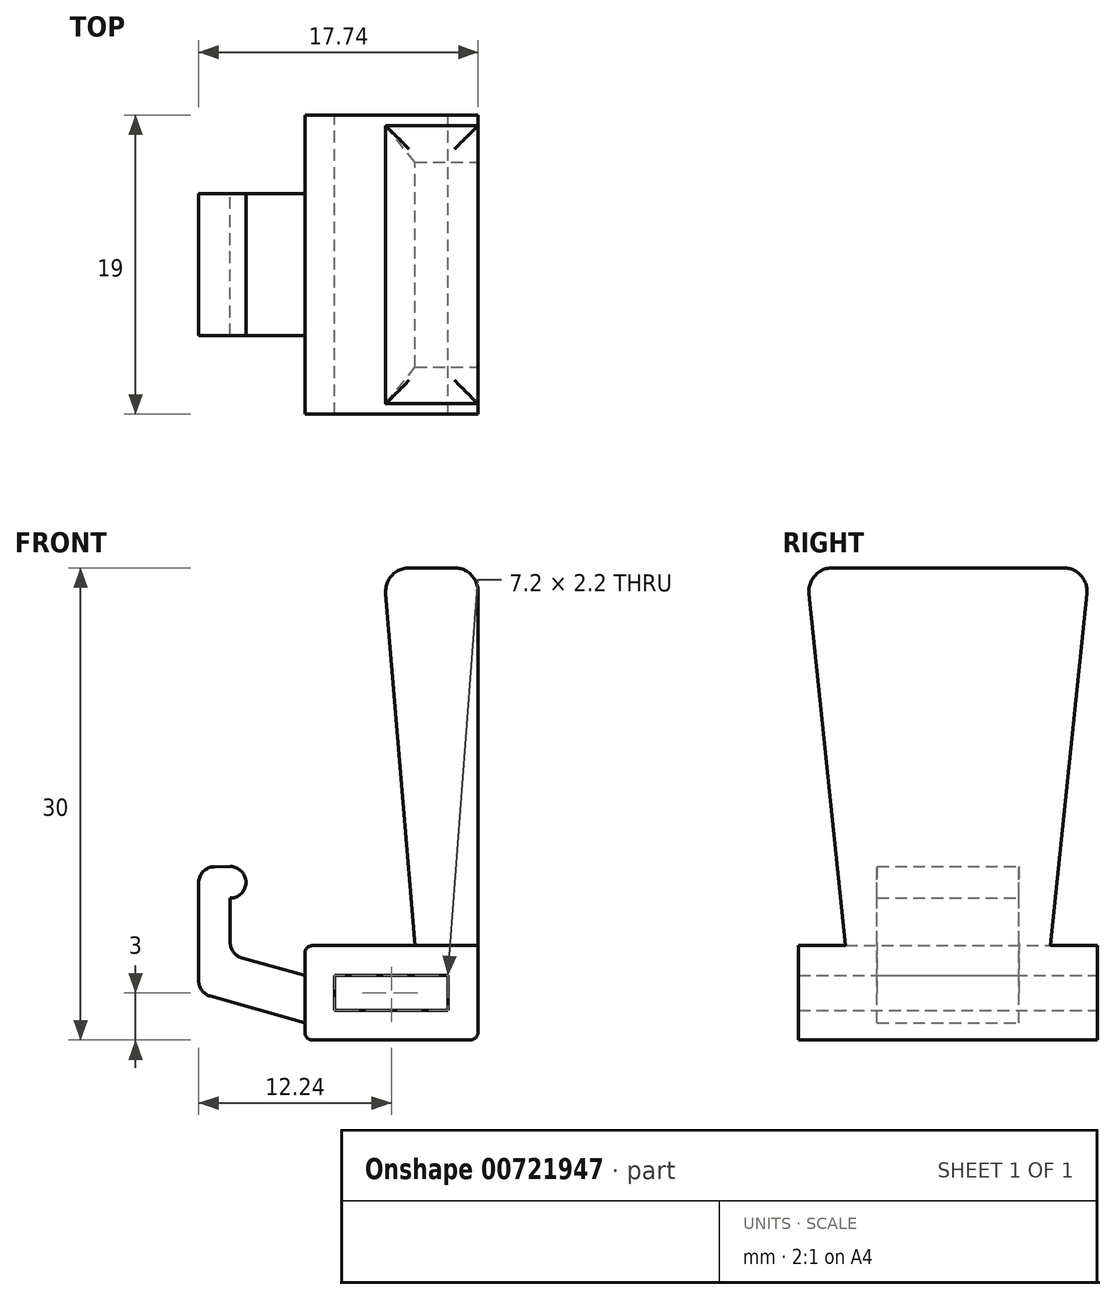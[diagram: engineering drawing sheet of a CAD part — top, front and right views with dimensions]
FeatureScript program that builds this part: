
annotation { "Feature Type Name" : "Feature", "Feature Type Description" : "" }
export const myFeature = defineFeature(function(context is Context, id is Id, definition is map)
    precondition{}
    {
        {
            var Q0;
            Q0=qCreatedBy(makeId("Front.planeOp"),FACE);
            var sketch = newSketch(context, id + "F0", { "sketchPlane" : qUnion([Q0])});
            skLineSegment(sketch, "E0.bottom", {"start": v(0, 0) * mm, "end": v(-11, 0) * mm});
            skLineSegment(sketch, "E0.top", {"start": v(0, 6) * mm, "end": v(-11, 6) * mm});
            skLineSegment(sketch, "E0.left", {"start": v(0, 0) * mm, "end": v(0, 6) * mm});
            skLineSegment(sketch, "E0.right", {"start": v(-11, 0) * mm, "end": v(-11, 6) * mm});
            skPoint(sketch, "E0.middle", {"position": v(-5.5, 3) * mm});
            skLineSegment(sketch, "E1.bottom", {"start": v(-1.9, 1.9) * mm, "end": v(-9.1, 1.9) * mm});
            skLineSegment(sketch, "E1.top", {"start": v(-1.9, 4.1) * mm, "end": v(-9.1, 4.1) * mm});
            skLineSegment(sketch, "E1.left", {"start": v(-1.9, 1.9) * mm, "end": v(-1.9, 4.1) * mm});
            skLineSegment(sketch, "E1.right", {"start": v(-9.1, 1.9) * mm, "end": v(-9.1, 4.1) * mm});
            skLineSegment(sketch, "E2", {"start": v(-11, 1.1) * mm, "end": v(-17.74, 3) * mm});
            skLineSegment(sketch, "E3", {"start": v(-17.74, 3) * mm, "end": v(-17.74, 6) * mm});
            skLineSegment(sketch, "E4", {"start": v(-17.74, 6) * mm, "end": v(-11, 4.1) * mm});
            skLineSegment(sketch, "E5", {"start": v(-17.74, 6) * mm, "end": v(-17.74, 11) * mm});
            skLineSegment(sketch, "E6", {"start": v(-15.74, 5.44) * mm, "end": v(-15.74, 11.02) * mm});
            skLineSegment(sketch, "E7", {"start": v(-15.74, 11.02) * mm, "end": v(-17.74, 11) * mm});
            skLineSegment(sketch, "E8", {"start": v(-15.74, 11.02) * mm, "end": v(-14.74, 11.02) * mm});
            skLineSegment(sketch, "E9", {"start": v(-14.74, 11.02) * mm, "end": v(-14.74, 9.02) * mm});
            skLineSegment(sketch, "E10", {"start": v(-14.74, 9.02) * mm, "end": v(-15.74, 9.02) * mm});
            skLineSegment(sketch, "E11", {"start": v(0, 6) * mm, "end": v(0, 30) * mm});
            skLineSegment(sketch, "E12", {"start": v(0, 30) * mm, "end": v(-6, 30) * mm});
            skLineSegment(sketch, "E13", {"start": v(-6, 30) * mm, "end": v(-4, 6) * mm});
            skLineSegment(sketch, "E14", {"start": v(-4, 6) * mm, "end": v(0, 6) * mm});
            skSolve(sketch);
        }
        {
            var Q0;
            {var subQ5=sQuery(id+"F0.wireOp",EDGE,"E0.bottom");Q0=makeQuery(id+"F0.imprint","IMPRINT",FACE,{"disambiguationData":[TD([[makeQuery(id+"F0.imprint","IMPRINT",EDGE,{"derivedFrom":subQ5}),-1.0]])]});}
            extrude(context, id + "F1", {"entities" : qUnion([Q0]), "endBound" : BoundingType.SYMMETRIC, "depth" : 19 * mm, "offsetDistance" : 25 * mm});
        }
        {
            var Q0;
            {var subQ0=sQuery(id+"F0.wireOp",EDGE,"E11");Q0=makeQuery(id+"F0.imprint","IMPRINT",FACE,{"disambiguationData":[TD([[makeQuery(id+"F0.imprint","IMPRINT",EDGE,{"derivedFrom":subQ0}),1.0]])]});}
            extrude(context, id + "F2", {"entities" : qUnion([Q0]), "operationType" : NewBodyOperationType.ADD, "endBound" : BoundingType.SYMMETRIC, "depth" : 18 * mm, "offsetDistance" : 25 * mm});
        }
        {
            var Q0;
            Q0=makeQuery(id+"F2.boolean.opBoolean","MERGE",FACE,{"derivedFrom":[makeQuery(id+"F1.opExtrude","SWEPT_FACE",FACE,{"disambiguationData":[OSD([sQuery(id+"F0.wireOp",EDGE,"E0.left")])]}),makeQuery(id+"F2.opExtrude","SWEPT_FACE",FACE,{"disambiguationData":[OSD([sQuery(id+"F0.wireOp",EDGE,"E11")])]})]});
            var sketch = newSketch(context, id + "F3", { "sketchPlane" : qUnion([Q0])});
            skLineSegment(sketch, "E15", {"start": v(9, 30) * mm, "end": v(-9, 30) * mm});
            skLineSegment(sketch, "E16", {"start": v(-9, 30) * mm, "end": v(-6.5, 6) * mm});
            skLineSegment(sketch, "E17", {"start": v(-6.5, 6) * mm, "end": v(6.5, 6) * mm});
            skLineSegment(sketch, "E18", {"start": v(6.5, 6) * mm, "end": v(9, 30) * mm});
            skLineSegment(sketch, "E19", {"start": v(-9, 6) * mm, "end": v(9, 6) * mm});
            skSolve(sketch);
        }
        {
            var Q0;
            Q0=makeQuery(id+"F3.imprint","IMPRINT",FACE,{"disambiguationData":[TD([[makeQuery(id+"F3.imprint","IMPRINT",EDGE,{"derivedFrom":sQuery(id+"F3.wireOp",EDGE,"E15")}),-1.0]])]});
            extrude(context, id + "F4", {"entities" : qUnion([Q0]), "operationType" : NewBodyOperationType.INTERSECT, "oppositeDirection" : true, "depth" : 11 * mm, "offsetDistance" : 25 * mm});
        }
        {
            var Q0;
            {var subQ4=sQuery(id+"F0.wireOp",EDGE,"E0.bottom");Q0=makeQuery(id+"F0.imprint","IMPRINT",FACE,{"disambiguationData":[TD([[makeQuery(id+"F0.imprint","IMPRINT",EDGE,{"derivedFrom":subQ4}),-1.0]])]});}
            extrude(context, id + "F5", {"entities" : qUnion([Q0]), "operationType" : NewBodyOperationType.ADD, "endBound" : BoundingType.SYMMETRIC, "depth" : 19 * mm, "offsetDistance" : 25 * mm});
        }
        {
            var Q0;
            {var subQ3=sQuery(id+"F0.wireOp",EDGE,"E2");Q0=makeQuery(id+"F0.imprint","IMPRINT",FACE,{"disambiguationData":[TD([[makeQuery(id+"F0.imprint","IMPRINT",EDGE,{"derivedFrom":subQ3}),-1.0]])]});}
            var Q1;
            {var subQ5=sQuery(id+"F0.wireOp",EDGE,"E5");Q1=makeQuery(id+"F0.imprint","IMPRINT",FACE,{"disambiguationData":[TD([[makeQuery(id+"F0.imprint","IMPRINT",EDGE,{"derivedFrom":subQ5}),-1.0]])]});}
            var Q2;
            {var subQ0=sQuery(id+"F0.wireOp",EDGE,"E8");Q2=makeQuery(id+"F0.imprint","IMPRINT",FACE,{"disambiguationData":[TD([[makeQuery(id+"F0.imprint","IMPRINT",EDGE,{"derivedFrom":subQ0}),-1.0]])]});}
            extrude(context, id + "F6", {"entities" : qUnion([Q0, Q1, Q2]), "operationType" : NewBodyOperationType.ADD, "endBound" : BoundingType.SYMMETRIC, "depth" : 9 * mm, "offsetDistance" : 25 * mm});
        }
        {
            var Q0;
            Q0=makeQuery(id+"F6.opExtrude","SWEPT_EDGE",EDGE,{"disambiguationData":[OSD([sQuery(id+"F0.wireOp",EDGE,"E5"),sQuery(id+"F0.wireOp",EDGE,"E7")])]});
            var Q1;
            Q1=makeQuery(id+"F6.opExtrude","SWEPT_EDGE",EDGE,{"disambiguationData":[OSD([sQuery(id+"F0.wireOp",EDGE,"E8"),sQuery(id+"F0.wireOp",EDGE,"E9")])]});
            var Q2;
            Q2=makeQuery(id+"F6.opExtrude","SWEPT_EDGE",EDGE,{"disambiguationData":[OSD([sQuery(id+"F0.wireOp",EDGE,"E9"),sQuery(id+"F0.wireOp",EDGE,"E10")])]});
            var Q3;
            Q3=makeQuery(id+"F6.opExtrude","SWEPT_EDGE",EDGE,{"disambiguationData":[OSD([sQuery(id+"F0.wireOp",EDGE,"E2"),sQuery(id+"F0.wireOp",EDGE,"E3")])]});
            var Q4;
            Q4=makeQuery(id+"F6.opExtrude","SWEPT_EDGE",EDGE,{"disambiguationData":[OSD([sQuery(id+"F0.wireOp",EDGE,"E4"),sQuery(id+"F0.wireOp",EDGE,"E6")])]});
            fillet(context, id + "F7", {"entities" : qUnion([Q0, Q1, Q2, Q3, Q4]), "radius" : 1 * mm, "tangentPropagation" : true, "allowEdgeOverflow" : false});
        }
        {
            var Q0;
            Q0=makeQuery(id+"F5.opExtrude","SWEPT_EDGE",EDGE,{"disambiguationData":[OSD([sQuery(id+"F0.wireOp",EDGE,"E0.top"),sQuery(id+"F0.wireOp",EDGE,"E0.right")])]});
            var Q1;
            {var subQ0=sQuery(id+"F0.wireOp",EDGE,"E11");var subQ1=sQuery(id+"F0.wireOp",EDGE,"E0.left");var subQ2=sQuery(id+"F0.wireOp",EDGE,"E14");Q1=makeQuery(id+"F5.boolean.opBoolean","SPLIT",EDGE,{"disambiguationData":[TD([makeQuery(id+"F4.boolean.opBoolean","COPY",FACE,{"derivedFrom":makeQuery(id+"F4.boolean.toolComplement.opBoolean","COPY",FACE,{"derivedFrom":makeQuery(id+"F4.opExtrude","SWEPT_FACE",FACE,{"disambiguationData":[OSD([sQuery(id+"F3.wireOp",EDGE,"E16")])]})})})])],"derivedFrom":makeQuery(id+"F5.opExtrude","SWEPT_EDGE",EDGE,{"disambiguationData":[OSD([subQ1,subQ0,subQ2])]})});}
            var Q2;
            {var subQ0=sQuery(id+"F0.wireOp",EDGE,"E14");var subQ1=sQuery(id+"F0.wireOp",EDGE,"E0.left");var subQ3=sQuery(id+"F0.wireOp",EDGE,"E11");Q2=makeQuery(id+"F5.boolean.opBoolean","SPLIT",EDGE,{"disambiguationData":[TD([makeQuery(id+"F4.boolean.opBoolean","COPY",FACE,{"derivedFrom":makeQuery(id+"F4.boolean.toolComplement.opBoolean","COPY",FACE,{"derivedFrom":makeQuery(id+"F4.opExtrude","SWEPT_FACE",FACE,{"disambiguationData":[OSD([sQuery(id+"F3.wireOp",EDGE,"E18")])]})})})])],"derivedFrom":makeQuery(id+"F5.opExtrude","SWEPT_EDGE",EDGE,{"disambiguationData":[OSD([subQ1,subQ3,subQ0])]})});}
            var Q3;
            Q3=makeQuery(id+"F5.opExtrude","SWEPT_EDGE",EDGE,{"disambiguationData":[OSD([sQuery(id+"F0.wireOp",EDGE,"E0.bottom"),sQuery(id+"F0.wireOp",EDGE,"E0.right")])]});
            var Q4;
            Q4=makeQuery(id+"F5.opExtrude","SWEPT_EDGE",EDGE,{"disambiguationData":[OSD([sQuery(id+"F0.wireOp",EDGE,"E0.bottom"),sQuery(id+"F0.wireOp",EDGE,"E0.left")])]});
            fillet(context, id + "F8", {"entities" : qUnion([Q0, Q1, Q2, Q3, Q4]), "radius" : 0.5 * mm, "tangentPropagation" : true, "allowEdgeOverflow" : false});
        }
        {
            var Q0;
            Q0=makeQuery(id+"F2.opExtrude","SWEPT_EDGE",EDGE,{"disambiguationData":[OSD([sQuery(id+"F0.wireOp",EDGE,"E12"),sQuery(id+"F0.wireOp",EDGE,"E13")])]});
            var Q1;
            Q1=makeQuery(id+"F2.opExtrude","SWEPT_EDGE",EDGE,{"disambiguationData":[OSD([sQuery(id+"F0.wireOp",EDGE,"E11"),sQuery(id+"F0.wireOp",EDGE,"E12")])]});
            var Q2;
            Q2=makeQuery(id+"F4.boolean.opBoolean","MERGE",EDGE,{"derivedFrom":[makeQuery(id+"F2.opExtrude","CAP_EDGE",EDGE,{"disambiguationData":[OSD([sQuery(id+"F0.wireOp",EDGE,"E12")])],"isStart":false}),makeQuery(id+"F4.boolean.toolComplement.opBoolean","COPY",EDGE,{"derivedFrom":makeQuery(id+"F4.opExtrude","SWEPT_EDGE",EDGE,{"disambiguationData":[OSD([sQuery(id+"F0.wireOp",EDGE,"E11"),sQuery(id+"F3.wireOp",EDGE,"E15"),sQuery(id+"F3.wireOp",EDGE,"E16")])]})})]});
            var Q3;
            Q3=makeQuery(id+"F4.boolean.opBoolean","MERGE",EDGE,{"derivedFrom":[makeQuery(id+"F2.opExtrude","CAP_EDGE",EDGE,{"disambiguationData":[OSD([sQuery(id+"F0.wireOp",EDGE,"E12")])],"isStart":true}),makeQuery(id+"F4.boolean.toolComplement.opBoolean","COPY",EDGE,{"derivedFrom":makeQuery(id+"F4.opExtrude","SWEPT_EDGE",EDGE,{"disambiguationData":[OSD([sQuery(id+"F0.wireOp",EDGE,"E11"),sQuery(id+"F3.wireOp",EDGE,"E15"),sQuery(id+"F3.wireOp",EDGE,"E18")])]})})]});
            var Q4;
            Q4=makeQuery(id+"F4.boolean.opBoolean","INTERSECT",EDGE,{"derivedFrom":[makeQuery(id+"F2.opExtrude","SWEPT_FACE",FACE,{"disambiguationData":[OSD([sQuery(id+"F0.wireOp",EDGE,"E13")])]}),makeQuery(id+"F4.boolean.toolComplement.opBoolean","COPY",FACE,{"derivedFrom":makeQuery(id+"F4.opExtrude","SWEPT_FACE",FACE,{"disambiguationData":[OSD([sQuery(id+"F3.wireOp",EDGE,"E16")])]})})]});
            var Q5;
            Q5=makeQuery(id+"F4.boolean.opBoolean","COPY",EDGE,{"derivedFrom":makeQuery(id+"F4.boolean.toolComplement.opBoolean","COPY",EDGE,{"derivedFrom":makeQuery(id+"F4.opExtrude","CAP_EDGE",EDGE,{"disambiguationData":[OSD([sQuery(id+"F3.wireOp",EDGE,"E16")])],"isStart":true})})});
            var Q6;
            Q6=makeQuery(id+"F4.boolean.opBoolean","COPY",EDGE,{"derivedFrom":makeQuery(id+"F4.boolean.toolComplement.opBoolean","COPY",EDGE,{"derivedFrom":makeQuery(id+"F4.opExtrude","CAP_EDGE",EDGE,{"disambiguationData":[OSD([sQuery(id+"F3.wireOp",EDGE,"E18")])],"isStart":true})})});
            var Q7;
            Q7=makeQuery(id+"F4.boolean.opBoolean","INTERSECT",EDGE,{"derivedFrom":[makeQuery(id+"F2.opExtrude","SWEPT_FACE",FACE,{"disambiguationData":[OSD([sQuery(id+"F0.wireOp",EDGE,"E13")])]}),makeQuery(id+"F4.boolean.toolComplement.opBoolean","COPY",FACE,{"derivedFrom":makeQuery(id+"F4.opExtrude","SWEPT_FACE",FACE,{"disambiguationData":[OSD([sQuery(id+"F3.wireOp",EDGE,"E18")])]})})]});
            fillet(context, id + "F9", {"entities" : qUnion([Q0, Q1, Q2, Q3, Q4, Q5, Q6, Q7]), "radius" : 1.5 * mm, "tangentPropagation" : true, "allowEdgeOverflow" : false});
        }
    });
